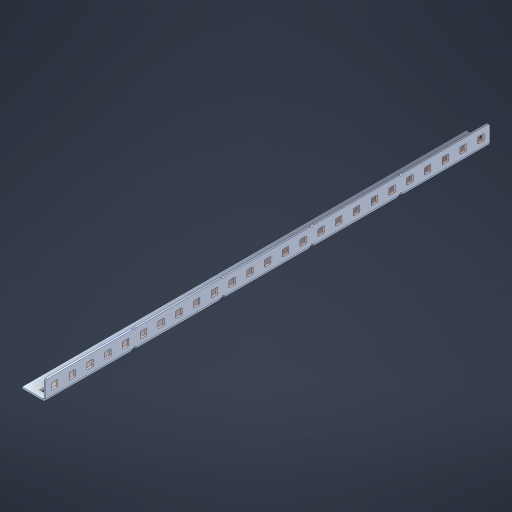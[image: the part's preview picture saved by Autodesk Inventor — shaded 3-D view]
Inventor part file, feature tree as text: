
AUTODESK INVENTOR PART (.ipt)
format: ipt  version: 2023 (Build 270158000, 158)  size: 846,848 bytes
history: native  units: in
note: dims shown in document units (in); Inventor stores cm internally (conversion verified against a paired STEP export)
features: other x55, extrude x49, sheet_metal_op x10, sketch x8, mirror x1, pattern_linear x1, chamfer x1
ambient origin geometry x8: Origin, YZ Plane, XZ Plane, XY Plane, X Axis, Y Axis, Z Axis, Center Point
bodies: Solid1 (feature_tree), Body (feature_tree)
feature tree (125):
  other  "Flange Pattern Plane"
  sheet_metal_op  "Flange Pattern"
  sheet_metal_op  "Body Pattern"
  other  "Arc Length"
  mirror  "Notch Mirror"
  pattern_linear  "Notch Pattern"  Spacing1=0.1875in  [1 undecoded]
  chamfer  "End Chamfer"
  extrude  "Half Cut"  Depth=0.0469in
  sketch  "Sketch1"  dims[d0=2.5in]
  other  "Plate1"
  sketch  "Sketch2"  dims[d1=12.5in]
  other  "Plate2"
  sheet_metal_op  "Bend1"
  sheet_metal_op  "Corner1"
  sketch  "Sketch3"  dims[d2=0.0469in]
  other  "Flange Pattern Sketch"
  sketch  "Sketch7"  dims[d3=0.0469in]
  other  "Srf1"
  other  "Srf2"
  sketch  "Sketch8"  dims[d4=0.0234in]
  sketch  "Sketch9"  dims[d5=0.0938in]
  other  "Srf91"
  sheet_metal_op  "Body Pattern Sketch"
  other  "Srf92"
  sketch  "Sketch13"  dims[d6=0.0469in]
  sketch  "Sketch14"  dims[d7=0.5in d8=90.0deg d9=0.0312in d10=0.1875in d11=0.0469in d12=0.0469in d16=0.182in d17=0.02in d18=0.0469in d19=0.0in d20=0.25in d21=0.25in d46=0.172in d47=1.0in d48=0.0in d49=0.182in d50=0.02in d51=0.25in d52=0.25in d53=0.0469in d54=0.0in d55=0.172in d56=1.0in d57=0.0in d60=9.8425in d62=0.5in d63=0.3937in d65=0.5in d85=0.1227in d86=0.1659in d88=0.04in d89=0.0469in d90=0.0in d91=0.04in d92=0.0491in d95=2.5in d96=0.04in d97=0.25in d98=45.0deg d101=0.0in d102=2.497in d131=0.5in d132=9.8425in d134=0.5in d139=0.5in]
  other  "Srf856"
  other  "Srf1310"
  other  "Srf1311"
  other  "Srf1312"
  other  "Srf1376"
  other  "Srf1377"
  other  "Srf1728"
  other  "Srf1755"
  other  "Srf1878"
  other  "Srf1879"
  other  "Srf1880"
  other  "Srf1881"
  other  "Srf1882"
  other  "Srf1883"
  other  "Srf1884"
  other  "Srf1885"
  other  "Srf1886"
  other  "Srf1887"
  other  "Srf1888"
  other  "Srf1889"
  other  "Srf1890"
  other  "Srf1891"
  other  "Srf1892"
  other  "Srf1893"
  other  "Srf1894"
  other  "Srf1895"
  other  "Srf1896"
  other  "Srf1942"
  other  "Srf1943"
  other  "Srf1944"
  other  "Srf1945"
  other  "Srf1946"
  other  "Srf1947"
  other  "Srf1948"
  other  "Srf1949"
  other  "Srf1950"
  other  "Srf1951"
  other  "Srf1952"
  other  "Srf1953"
  other  "Srf1954"
  other  "Srf1955"
  other  "Srf1956"
  other  "Srf1957"
  other  "Srf1958"
  other  "Srf1959"
  other  "Srf1960"
  sheet_metal_op  "Flange Stamp"
  sheet_metal_op  "Flange Circle"
  sheet_metal_op  "Body Stamp"
  sheet_metal_op  "Body Circle"
  sheet_metal_op  "Notch"
  extrude  "ExtrusionSrf2"  Depth=0.0469in
  extrude  "ExtrusionSrf92"  Depth=0.5in
  extrude  "ExtrusionSrf856"  Depth=0.02in
  extrude  "ExtrusionSrf1310"  Depth=0.0469in
  extrude  "ExtrusionSrf1311"  TaperAngle=0.0deg  [1 undecoded]
  extrude  "ExtrusionSrf1312"  Depth=0.5in
  extrude  "ExtrusionSrf1376"  Depth=0.5in
  extrude  "ExtrusionSrf1377"  Depth=0.5in
  extrude  "ExtrusionSrf1728"  Depth=0.5in TaperAngle=0.0deg
  extrude  "ExtrusionSrf1755"  Depth=0.5in
  extrude  "ExtrusionSrf1878"  Depth=0.02in
  extrude  "ExtrusionSrf1879"  Depth=0.5in
  extrude  "ExtrusionSrf1880"  Depth=0.5in
  extrude  "ExtrusionSrf1881"  Depth=0.0469in
  extrude  "ExtrusionSrf1882"  TaperAngle=0.0deg  [1 undecoded]
  extrude  "ExtrusionSrf1883"  Depth=0.5in
  extrude  "ExtrusionSrf1884"  Depth=0.5in TaperAngle=0.0deg
  extrude  "ExtrusionSrf1885"  Depth=0.5in
  extrude  "ExtrusionSrf1886"  Depth=0.5in
  extrude  "ExtrusionSrf1887"  Depth=0.5in
  extrude  "ExtrusionSrf1888"  Depth=0.5in
  extrude  "ExtrusionSrf1889"  Depth=0.5in
  extrude  "ExtrusionSrf1890"  Depth=0.0469in
  extrude  "ExtrusionSrf1891"  TaperAngle=0.0deg  [1 undecoded]
  extrude  "ExtrusionSrf1892"  Depth=0.5in
  extrude  "ExtrusionSrf1893"  Depth=0.5in
  extrude  "ExtrusionSrf1894"  Depth=0.5in
  extrude  "ExtrusionSrf1895"  Depth=0.5in TaperAngle=45.0deg
  extrude  "ExtrusionSrf1896"  TaperAngle=0.0deg  [1 undecoded]
  extrude  "ExtrusionSrf1942"  Depth=0.5in
  extrude  "ExtrusionSrf1943"  Depth=0.5in
  extrude  "ExtrusionSrf1944"  Depth=0.5in
  extrude  "ExtrusionSrf1945"  Depth=0.5in
  extrude  "ExtrusionSrf1946"  Depth=0.5in
  extrude  "ExtrusionSrf1947"  [1 undecoded]
  extrude  "ExtrusionSrf1948"  [1 undecoded]
  extrude  "ExtrusionSrf1949"  [1 undecoded]
  extrude  "ExtrusionSrf1950"  [1 undecoded]
  extrude  "ExtrusionSrf1951"  [1 undecoded]
  extrude  "ExtrusionSrf1952"  [1 undecoded]
  extrude  "ExtrusionSrf1953"  [1 undecoded]
  extrude  "ExtrusionSrf1954"  [1 undecoded]
  extrude  "ExtrusionSrf1955"  [1 undecoded]
  extrude  "ExtrusionSrf1956"  [1 undecoded]
  extrude  "ExtrusionSrf1957"  [1 undecoded]
  extrude  "ExtrusionSrf1958"  [1 undecoded]
  extrude  "ExtrusionSrf1959"  [1 undecoded]
  extrude  "ExtrusionSrf1960"  [1 undecoded]
note: 19 required parameter values undecoded (feature->parameter linkage not recoverable at this tier; creation-order binding heuristic only, values carry confidence <= 0.55)
